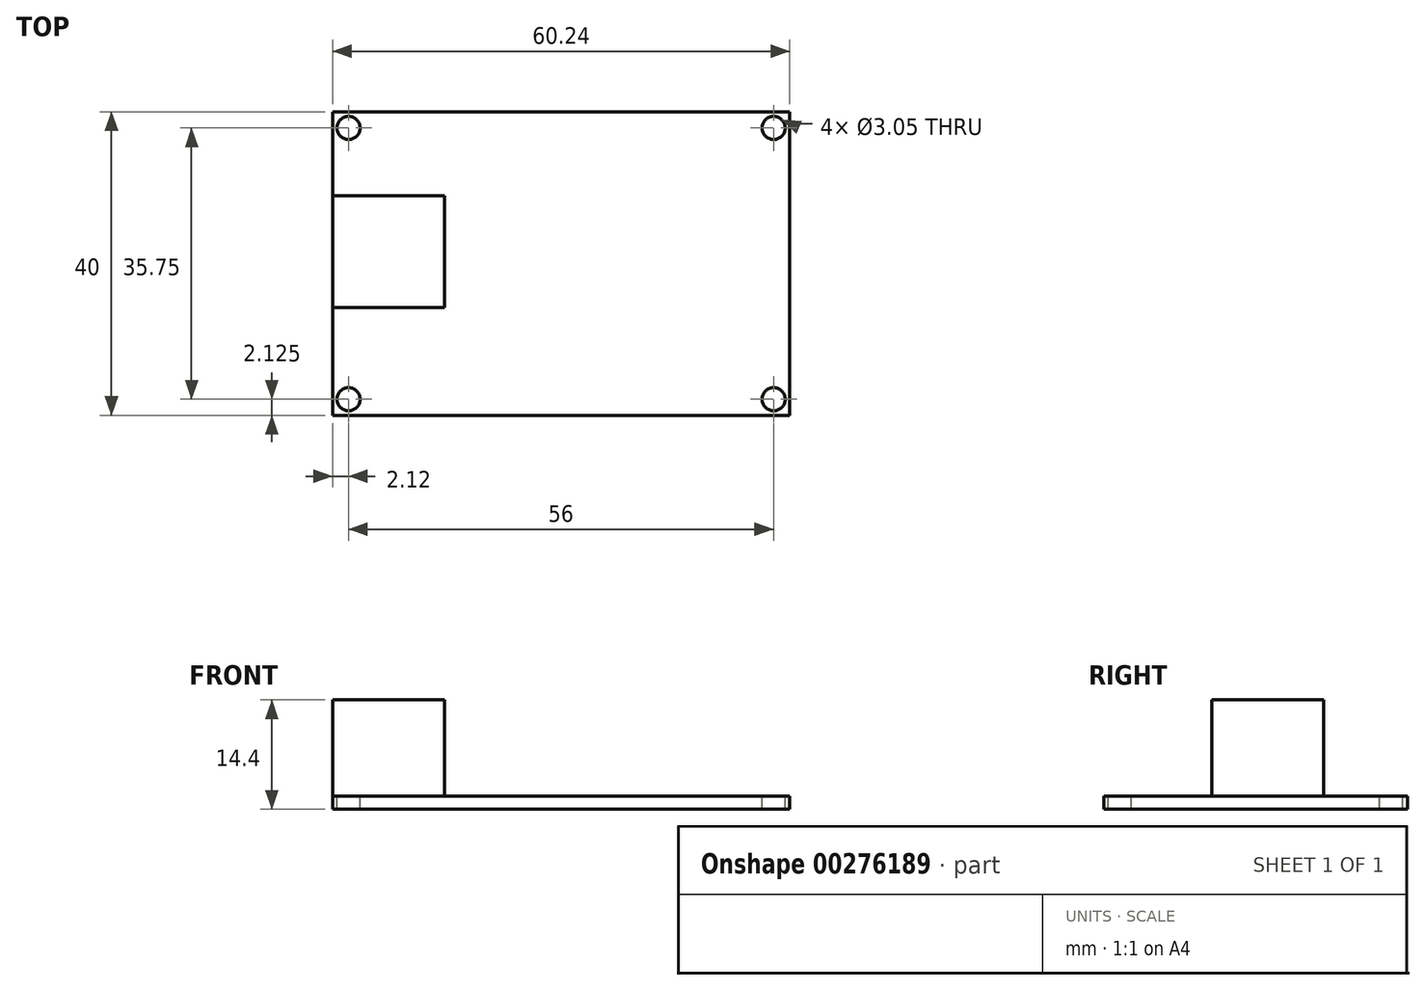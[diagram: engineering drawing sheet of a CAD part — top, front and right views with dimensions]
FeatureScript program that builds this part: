
annotation { "Feature Type Name" : "Feature", "Feature Type Description" : "" }
export const myFeature = defineFeature(function(context is Context, id is Id, definition is map)
    precondition{}
    {
        {
            var Q0;
            Q0=qCreatedBy(makeId("Top.planeOp"),FACE);
            var sketch = newSketch(context, id + "F0", { "sketchPlane" : qUnion([Q0])});
            skLineSegment(sketch, "E0.bottom", {"start": v(30.12, 20) * mm, "end": v(-30.12, 20) * mm});
            skLineSegment(sketch, "E0.top", {"start": v(30.12, -20) * mm, "end": v(-30.12, -20) * mm});
            skLineSegment(sketch, "E0.left", {"start": v(30.12, 20) * mm, "end": v(30.12, -20) * mm});
            skLineSegment(sketch, "E0.right", {"start": v(-30.12, 20) * mm, "end": v(-30.12, -20) * mm});
            skPoint(sketch, "E0.middle", {"position": v(0, 0) * mm});
            skSolve(sketch);
        }
        {
            var Q0;
            Q0=qSketchRegion(id+"F0",true);
            extrude(context, id + "F1", {"entities" : qUnion([Q0]), "depth" : 1.7 * mm});
        }
        {
            var Q0;
            Q0=makeQuery(id+"F1.opExtrude","CAP_FACE",FACE,{"disambiguationData":[OSD([sQuery(id+"F0.wireOp",EDGE,"E0.bottom"),sQuery(id+"F0.wireOp",EDGE,"E0.top"),sQuery(id+"F0.wireOp",EDGE,"E0.left"),sQuery(id+"F0.wireOp",EDGE,"E0.right")])],"isStart":false});
            var sketch = newSketch(context, id + "F2", { "sketchPlane" : qUnion([Q0])});
            skLineSegment(sketch, "E1.bottom", {"start": v(28, 17.88) * mm, "end": v(-28, 17.88) * mm, "construction": true});
            skLineSegment(sketch, "E1.top", {"start": v(28, -17.88) * mm, "end": v(-28, -17.88) * mm, "construction": true});
            skLineSegment(sketch, "E1.left", {"start": v(28, 17.88) * mm, "end": v(28, -17.88) * mm, "construction": true});
            skLineSegment(sketch, "E1.right", {"start": v(-28, 17.88) * mm, "end": v(-28, -17.88) * mm, "construction": true});
            skPoint(sketch, "E1.middle", {"position": v(0, 0) * mm});
            skCircle(sketch, "E2", {"center": v(-28, 17.88) * mm, "radius": 1.52 * mm});
            skCircle(sketch, "E3", {"center": v(28, 17.88) * mm, "radius": 1.52 * mm});
            skCircle(sketch, "E4", {"center": v(28, -17.88) * mm, "radius": 1.52 * mm});
            skCircle(sketch, "E5", {"center": v(-28, -17.88) * mm, "radius": 1.52 * mm});
            skSolve(sketch);
        }
        {
            var Q0;
            Q0=qSketchRegion(id+"F2",true);
            extrude(context, id + "F3", {"entities" : qUnion([Q0]), "operationType" : NewBodyOperationType.REMOVE, "endBound" : BoundingType.THROUGH_ALL, "oppositeDirection" : true, "depth" : 25.4 * mm});
        }
        {
            var Q0;
            Q0=makeQuery(id+"F1.opExtrude","CAP_FACE",FACE,{"disambiguationData":[OSD([sQuery(id+"F0.wireOp",EDGE,"E0.bottom"),sQuery(id+"F0.wireOp",EDGE,"E0.top"),sQuery(id+"F0.wireOp",EDGE,"E0.left"),sQuery(id+"F0.wireOp",EDGE,"E0.right")])],"isStart":false});
            var sketch = newSketch(context, id + "F4", { "sketchPlane" : qUnion([Q0])});
            skLineSegment(sketch, "E6.bottom", {"start": v(-30.12, -5.77) * mm, "end": v(-15.4, -5.77) * mm});
            skLineSegment(sketch, "E6.top", {"start": v(-30.12, 8.97) * mm, "end": v(-15.4, 8.97) * mm});
            skLineSegment(sketch, "E6.left", {"start": v(-30.12, -5.77) * mm, "end": v(-30.12, 8.97) * mm});
            skLineSegment(sketch, "E6.right", {"start": v(-15.4, -5.77) * mm, "end": v(-15.4, 8.97) * mm});
            skPoint(sketch, "E7", {"position": v(-30.12, 1.6) * mm});
            skSolve(sketch);
        }
        {
            var Q0;
            Q0=qSketchRegion(id+"F4",true);
            extrude(context, id + "F5", {"entities" : qUnion([Q0]), "operationType" : NewBodyOperationType.ADD, "depth" : 12.7 * mm});
        }
    });
